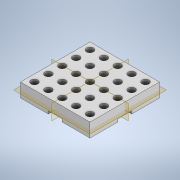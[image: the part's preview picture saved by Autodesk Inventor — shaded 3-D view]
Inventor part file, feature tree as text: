
AUTODESK INVENTOR PART (.ipt)
format: ipt  version: 2022.4 (Build 264492010, 492A)  size: 222,208 bytes
history: native  units: mm
features: extrude x4, sketch x3
ambient origin geometry x8: Origin, YZ Plane, XZ Plane, XY Plane, X Axis, Y Axis, Z Axis, Center Point
bodies: Solid1 (feature_tree)
feature tree (7):
  extrude  "Extrusion1"  Depth=50.0mm
  sketch  "Sketch2"  dims[d2=10.0mm d3=0.0mm d4=10.0mm]
  extrude  "Extrusion2"  Depth=10.0mm
  extrude  "Extrusion3"  Depth=3.0mm
  extrude  "Extrusion4"  Depth=40.0mm TaperAngle=360.0deg
  sketch  "Sketch1"  dims[d0=50.0mm d1=50.0mm]
  sketch  "Sketch3"  dims[d5=8.0mm d6=3.0mm d7=40.0mm d9=360.0deg d11=2.0mm d12=0.0mm d13=4.0mm d14=0.0mm d15=5.0mm d16=5.0mm d17=5.0mm d18=50.0mm d20=10.0mm d21=50.0mm d23=10.0mm d26=5.0mm d27=0.0mm]
